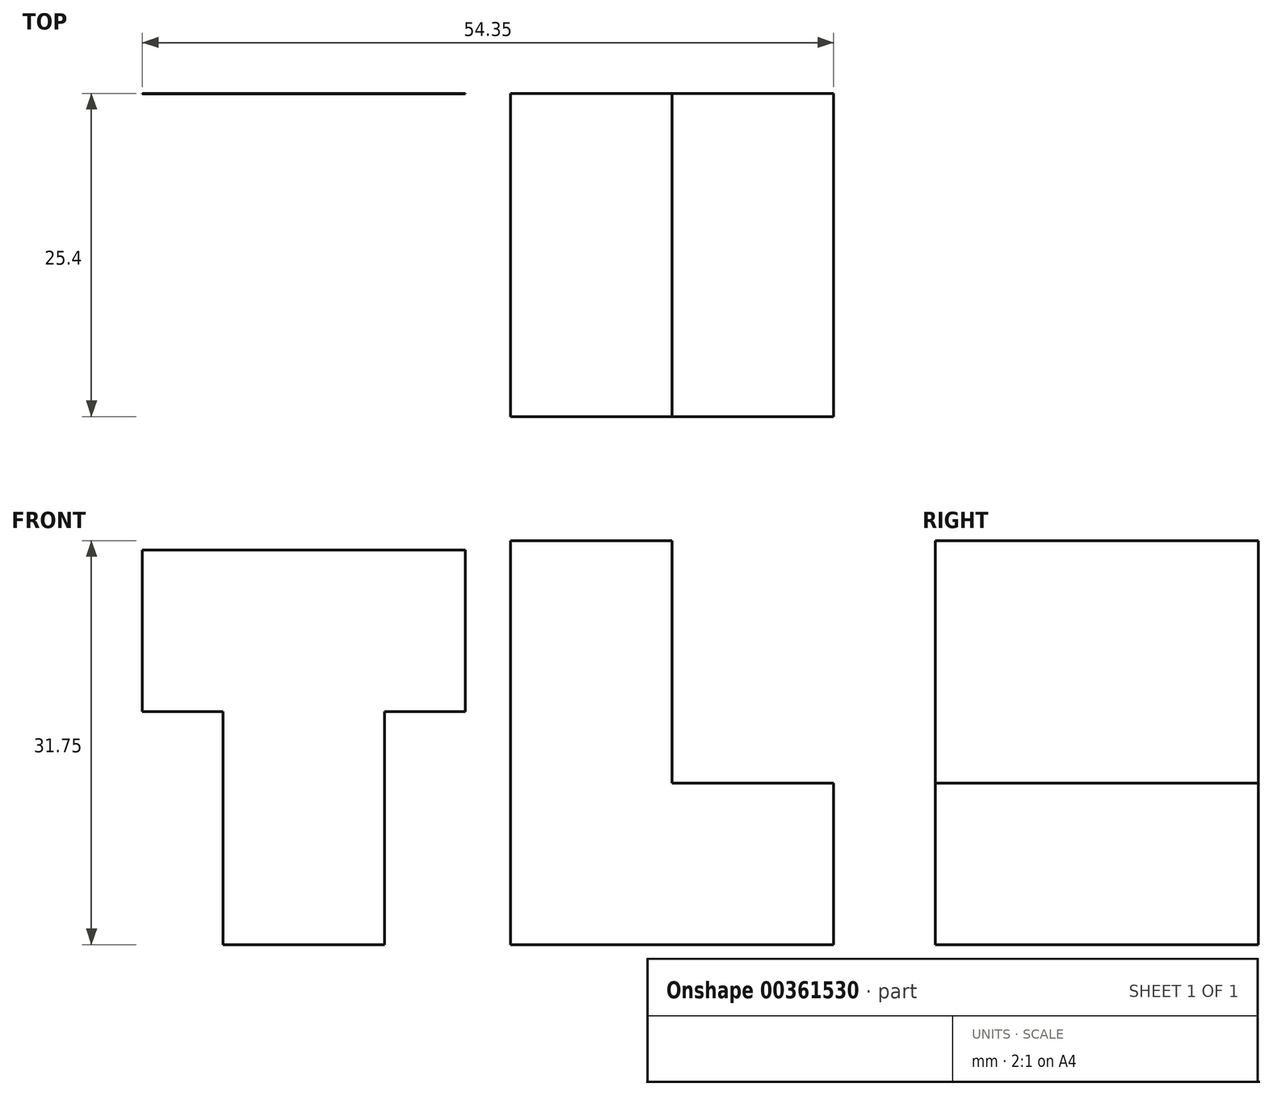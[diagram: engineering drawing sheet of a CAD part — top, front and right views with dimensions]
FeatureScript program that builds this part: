
annotation { "Feature Type Name" : "Feature", "Feature Type Description" : "" }
export const myFeature = defineFeature(function(context is Context, id is Id, definition is map)
    precondition{}
    {
        {
            var Q0;
            Q0=qCreatedBy(makeId("Front.planeOp"),FACE);
            var sketch = newSketch(context, id + "F0", { "sketchPlane" : qUnion([Q0])});
            skLineSegment(sketch, "E0", {"start": v(0, 31.75) * mm, "end": v(0, 0) * mm});
            skLineSegment(sketch, "E1", {"start": v(0, 0) * mm, "end": v(25.4, 0) * mm});
            skLineSegment(sketch, "E2", {"start": v(25.4, 0) * mm, "end": v(25.4, 12.7) * mm});
            skLineSegment(sketch, "E3", {"start": v(25.4, 12.7) * mm, "end": v(12.7, 12.7) * mm});
            skLineSegment(sketch, "E4", {"start": v(12.7, 12.7) * mm, "end": v(12.7, 31.75) * mm});
            skLineSegment(sketch, "E5", {"start": v(12.7, 31.75) * mm, "end": v(0, 31.75) * mm});
            skSolve(sketch);
        }
        {
            var Q0;
            Q0=makeQuery(id+"F0.imprint","IMPRINT",FACE,{"disambiguationData":[TD([[makeQuery(id+"F0.imprint","IMPRINT",EDGE,{"derivedFrom":sQuery(id+"F0.wireOp",EDGE,"E0")}),1.0]])]});
            extrude(context, id + "F1", {"entities" : qUnion([Q0]), "depth" : 25.4 * mm});
        }
        {
            var Q0;
            Q0=qCreatedBy(makeId("Front.planeOp"),FACE);
            var sketch = newSketch(context, id + "F2", { "sketchPlane" : qUnion([Q0])});
            skLineSegment(sketch, "E6", {"start": v(-9.9, 0) * mm, "end": v(-9.9, 18.31) * mm});
            skLineSegment(sketch, "E7", {"start": v(-9.9, 18.31) * mm, "end": v(-3.55, 18.31) * mm});
            skLineSegment(sketch, "E8", {"start": v(-3.55, 18.31) * mm, "end": v(-3.55, 31.01) * mm});
            skLineSegment(sketch, "E9", {"start": v(-3.55, 31.01) * mm, "end": v(-28.95, 31.01) * mm});
            skLineSegment(sketch, "E10", {"start": v(-28.95, 31.01) * mm, "end": v(-28.95, 18.31) * mm});
            skLineSegment(sketch, "E11", {"start": v(-28.95, 18.31) * mm, "end": v(-22.6, 18.31) * mm});
            skLineSegment(sketch, "E12", {"start": v(-22.6, 18.31) * mm, "end": v(-22.6, 0) * mm});
            skLineSegment(sketch, "E13", {"start": v(-22.6, 0) * mm, "end": v(-9.9, 0) * mm});
            skSolve(sketch);
        }
        {
            var Q0;
            Q0=makeQuery(id+"F2.imprint","IMPRINT",FACE,{"disambiguationData":[TD([[makeQuery(id+"F2.imprint","IMPRINT",EDGE,{"derivedFrom":sQuery(id+"F2.wireOp",EDGE,"E6")}),1.0]])]});
            extrude(context, id + "F3", {"entities" : qUnion([Q0]), "depth" : 5 / 101.6 * mm});
        }
    });
